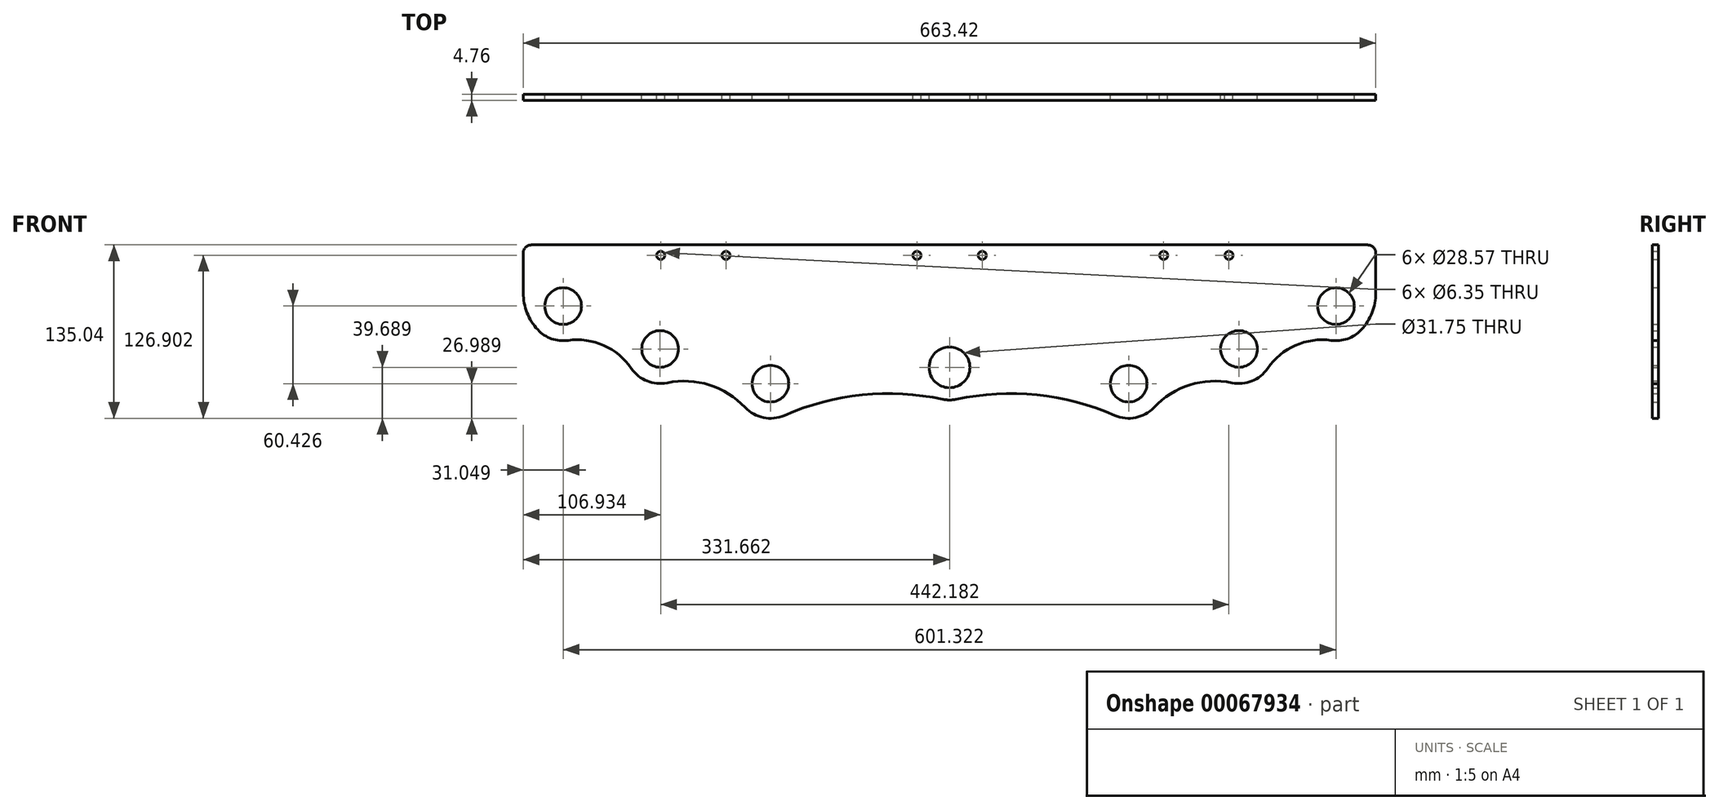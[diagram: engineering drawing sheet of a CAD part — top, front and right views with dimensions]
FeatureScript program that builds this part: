
annotation { "Feature Type Name" : "Feature", "Feature Type Description" : "" }
export const myFeature = defineFeature(function(context is Context, id is Id, definition is map)
    precondition{}
    {
        {
            var Q0;
            Q0=qCreatedBy(makeId("Front.planeOp"),FACE);
            var sketch = newSketch(context, id + "F0", { "sketchPlane" : qUnion([Q0])});
            skLineSegment(sketch, "E0", {"start": v(678.42, -37.96) * mm, "end": v(-454, -37.96) * mm, "construction": true});
            skCircle(sketch, "E1", {"center": v(300.66, 73.27) * mm, "radius": 41.28 * mm, "construction": true});
            skLineSegment(sketch, "E2", {"start": v(0, -37.96) * mm, "end": v(0, 332.54) * mm, "construction": true});
            skCircle(sketch, "E3", {"center": v(300.66, 73.27) * mm, "radius": 14.29 * mm});
            skCircle(sketch, "E4", {"center": v(217.4, 112.75) * mm, "radius": 3.18 * mm});
            skCircle(sketch, "E5", {"center": v(166.6, 112.75) * mm, "radius": 3.18 * mm});
            skCircle(sketch, "E6", {"center": v(25.4, 112.75) * mm, "radius": 3.18 * mm});
            skLineSegment(sketch, "E7", {"start": v(331.7, 83.55) * mm, "end": v(331.7, 114.54) * mm});
            skPoint(sketch, "E8.visualSharp", {"position": v(331.7, 119.1) * mm});
            skArc(sketch, "E8.filletArc", {"start": v(331.7, 114.54) * mm, "mid": v(329.85, 119.03) * mm, "end": v(325.36, 120.9) * mm});
            skPoint(sketch, "E9.third.point", {"position": v(216.25, -1.48) * mm});
            skPoint(sketch, "E10.orphan", {"position": v(0, -22.86) * mm});
            skCircle(sketch, "E11", {"center": v(300.66, 73.27) * mm, "radius": 21 * mm, "construction": true});
            skCircle(sketch, "E12", {"center": v(-0.05, 25.54) * mm, "radius": 41.28 * mm, "construction": true});
            skCircle(sketch, "E13.MirrorC", {"center": v(-0.05, 25.54) * mm, "radius": 15.88 * mm});
            skLineSegment(sketch, "E14", {"start": v(325.36, 120.9) * mm, "end": v(0, 120.9) * mm});
            skLineSegment(sketch, "E15.MirrorCS", {"start": v(-325.36, 120.9) * mm, "end": v(0, 120.9) * mm});
            skArc(sketch, "E16.MirrorCS", {"start": v(-331.7, 114.54) * mm, "mid": v(-329.85, 119.03) * mm, "end": v(-325.36, 120.9) * mm});
            skLineSegment(sketch, "E17.MirrorCS", {"start": v(-331.7, 83.55) * mm, "end": v(-331.7, 114.54) * mm});
            skCircle(sketch, "E18.MirrorC", {"center": v(-25.4, 112.75) * mm, "radius": 3.18 * mm});
            skCircle(sketch, "E19.MirrorC", {"center": v(-173.98, 112.75) * mm, "radius": 3.18 * mm});
            skCircle(sketch, "E20.MirrorC", {"center": v(-224.78, 112.75) * mm, "radius": 3.18 * mm});
            skCircle(sketch, "E21", {"center": v(225.21, 39.9) * mm, "radius": 50.8 * mm, "construction": true});
            skCircle(sketch, "E22", {"center": v(139.38, 12.84) * mm, "radius": 50.8 * mm, "construction": true});
            skLineSegment(sketch, "E23", {"start": v(338.06, -37.96) * mm, "end": v(720.92, -140.55) * mm, "construction": true});
            skLineSegment(sketch, "E24", {"start": v(338.06, -37.96) * mm, "end": v(354.5, 23.38) * mm, "construction": true});
            skLineSegment(sketch, "E25", {"start": v(354.5, 23.38) * mm, "end": v(391.3, 13.51) * mm, "construction": true});
            skLineSegment(sketch, "E26", {"start": v(391.3, 13.51) * mm, "end": v(374.86, -47.82) * mm, "construction": true});
            skLineSegment(sketch, "E27", {"start": v(338.06, -37.96) * mm, "end": v(368.5, 75.63) * mm, "construction": true});
            skLineSegment(sketch, "E28", {"start": v(368.5, 75.63) * mm, "end": v(497.3, 41.12) * mm, "construction": true});
            skLineSegment(sketch, "E29", {"start": v(497.3, 41.12) * mm, "end": v(466.86, -72.47) * mm, "construction": true});
            skLineSegment(sketch, "E30", {"start": v(338.06, -37.96) * mm, "end": v(1103.17, -37.96) * mm});
            skCircle(sketch, "E31", {"center": v(225.21, 39.9) * mm, "radius": 14.29 * mm});
            skCircle(sketch, "E32", {"center": v(225.21, 39.9) * mm, "radius": 21 * mm, "construction": true});
            skCircle(sketch, "E33", {"center": v(139.38, 12.84) * mm, "radius": 14.29 * mm});
            skCircle(sketch, "E34", {"center": v(139.38, 12.84) * mm, "radius": 21 * mm, "construction": true});
            skCircle(sketch, "E35", {"center": v(-0.05, 25.54) * mm, "radius": 140 * mm, "construction": true});
            skCircle(sketch, "E36", {"center": v(139.38, 12.84) * mm, "radius": 90 * mm, "construction": true});
            skCircle(sketch, "E37", {"center": v(225.21, 39.9) * mm, "radius": 82.5 * mm, "construction": true});
            skLineSegment(sketch, "E38", {"start": v(225.21, 39.9) * mm, "end": v(300.66, 73.27) * mm, "construction": true});
            skLineSegment(sketch, "E39", {"start": v(262.94, 56.58) * mm, "end": v(269.1, 42.64) * mm, "construction": true});
            skArc(sketch, "E40.0", {"start": v(296.93, 46.54) * mm, "mid": v(309.67, 47.83) * mm, "end": v(320.38, 54.84) * mm});
            skArc(sketch, "E41.0", {"start": v(219.7, 13.48) * mm, "mid": v(235.3, 14.87) * mm, "end": v(247.5, 24.67) * mm});
            skArc(sketch, "E42.0", {"start": v(142.71, 39.62) * mm, "mid": v(140.97, 39.78) * mm, "end": v(139.22, 39.83) * mm});
            skCircle(sketch, "E43", {"center": v(-0.05, 25.54) * mm, "radius": 21 * mm, "construction": true});
            skArc(sketch, "E44.0", {"start": v(5.22, 0.7) * mm, "mid": v(2.62, 0.28) * mm, "end": v(0, 0.14) * mm});
            skArc(sketch, "E45", {"start": v(296.93, 46.54) * mm, "mid": v(269.1, 42.64) * mm, "end": v(247.5, 24.67) * mm});
            skLineSegment(sketch, "E46", {"start": v(139.38, 12.84) * mm, "end": v(225.21, 39.9) * mm, "construction": true});
            skLineSegment(sketch, "E47", {"start": v(182.3, 26.37) * mm, "end": v(186.87, 11.83) * mm});
            skArc(sketch, "E48", {"start": v(219.7, 13.48) * mm, "mid": v(186.87, 11.83) * mm, "end": v(159.03, -5.65) * mm});
            skLineSegment(sketch, "E49", {"start": v(-0.05, 25.54) * mm, "end": v(139.38, 12.84) * mm, "construction": true});
            skLineSegment(sketch, "E50", {"start": v(69.66, 19.19) * mm, "end": v(68.28, 4.01) * mm});
            skArc(sketch, "E51", {"start": v(128.56, -11.89) * mm, "mid": v(67.88, 4.05) * mm, "end": v(5.22, 0.7) * mm});
            skArc(sketch, "E52", {"start": v(320.38, 54.84) * mm, "mid": v(328.77, 68.12) * mm, "end": v(331.7, 83.55) * mm});
            skArc(sketch, "E53.trimOffspring", {"start": v(128.56, -11.89) * mm, "mid": v(144.79, -13.6) * mm, "end": v(159.03, -5.65) * mm});
            skCircle(sketch, "E54.MirrorC", {"center": v(-139.38, 12.84) * mm, "radius": 14.29 * mm});
            skCircle(sketch, "E55.MirrorC", {"center": v(-225.21, 39.9) * mm, "radius": 14.29 * mm});
            skCircle(sketch, "E56.MirrorC", {"center": v(-300.66, 73.27) * mm, "radius": 14.29 * mm});
            skArc(sketch, "E57.MirrorCS", {"start": v(-320.38, 54.84) * mm, "mid": v(-328.77, 68.12) * mm, "end": v(-331.7, 83.55) * mm});
            skArc(sketch, "E58.MirrorCS", {"start": v(-296.93, 46.54) * mm, "mid": v(-309.67, 47.83) * mm, "end": v(-320.38, 54.84) * mm});
            skArc(sketch, "E59.MirrorCS", {"start": v(-296.93, 46.54) * mm, "mid": v(-269.1, 42.64) * mm, "end": v(-247.5, 24.67) * mm});
            skArc(sketch, "E60.MirrorCS", {"start": v(-219.7, 13.48) * mm, "mid": v(-235.3, 14.87) * mm, "end": v(-247.5, 24.67) * mm});
            skArc(sketch, "E61.MirrorCS", {"start": v(-219.7, 13.48) * mm, "mid": v(-186.87, 11.83) * mm, "end": v(-159.03, -5.65) * mm});
            skArc(sketch, "E62.MirrorCS", {"start": v(-128.56, -11.89) * mm, "mid": v(-144.79, -13.6) * mm, "end": v(-159.03, -5.65) * mm});
            skArc(sketch, "E63.MirrorCS", {"start": v(-128.56, -11.89) * mm, "mid": v(-67.88, 4.05) * mm, "end": v(-5.22, 0.7) * mm});
            skCircle(sketch, "E64.MirrorC", {"center": v(-139.38, 12.84) * mm, "radius": 50.8 * mm, "construction": true});
            skCircle(sketch, "E65.MirrorC", {"center": v(-225.21, 39.9) * mm, "radius": 50.8 * mm, "construction": true});
            skCircle(sketch, "E66.MirrorC", {"center": v(-300.66, 73.27) * mm, "radius": 41.28 * mm, "construction": true});
            skArc(sketch, "E67.MirrorCS", {"start": v(-5.22, 0.7) * mm, "mid": v(-2.62, 0.28) * mm, "end": v(0, 0.14) * mm});
            skSolve(sketch);
        }
        {
            var Q0;
            Q0=makeQuery(id+"F0.imprint","IMPRINT",FACE,{"disambiguationData":[TD([[makeQuery(id+"F0.imprint","IMPRINT",EDGE,{"derivedFrom":sQuery(id+"F0.wireOp",EDGE,"E3")}),-1.0]])]});
            extrude(context, id + "F1", {"entities" : qUnion([Q0]), "depth" : 4.76 * mm});
        }
    });
